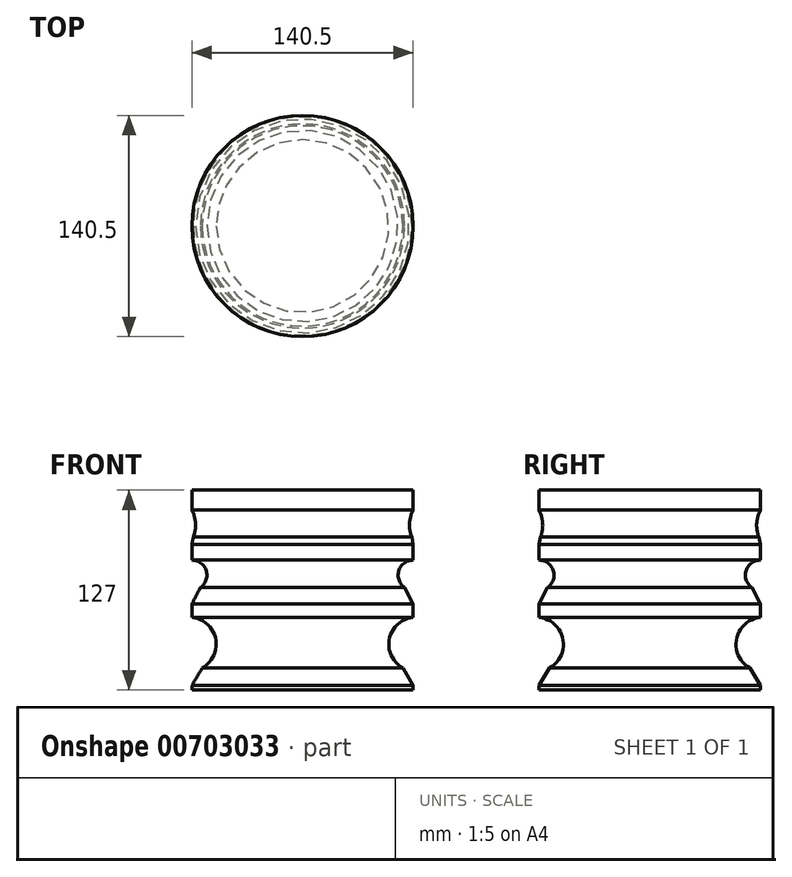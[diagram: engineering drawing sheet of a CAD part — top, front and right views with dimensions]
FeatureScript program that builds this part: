
annotation { "Feature Type Name" : "Feature", "Feature Type Description" : "" }
export const myFeature = defineFeature(function(context is Context, id is Id, definition is map)
    precondition{}
    {
        {
            var Q0;
            Q0=qCreatedBy(makeId("Front.planeOp"),FACE);
            var sketch = newSketch(context, id + "F0", { "sketchPlane" : qUnion([Q0])});
            skLineSegment(sketch, "E0", {"start": v(70.25, 0) * mm, "end": v(0, 0) * mm});
            skLineSegment(sketch, "E1", {"start": v(0, 0) * mm, "end": v(0, 127) * mm});
            skLineSegment(sketch, "E2", {"start": v(0, 127) * mm, "end": v(70.25, 127) * mm});
            skLineSegment(sketch, "E3", {"start": v(70.25, 127) * mm, "end": v(70.25, 114.3) * mm});
            skArc(sketch, "E4", {"start": v(70.25, 114.3) * mm, "mid": v(67.94, 104.78) * mm, "end": v(70.25, 95.25) * mm});
            skArc(sketch, "E5", {"start": v(70.25, 82.55) * mm, "mid": v(60.72, 73.03) * mm, "end": v(70.25, 63.5) * mm});
            skArc(sketch, "E6", {"start": v(70.25, 46.2) * mm, "mid": v(54.79, 29.12) * mm, "end": v(70.25, 12.04) * mm});
            skLineSegment(sketch, "E7.trimOffspring", {"start": v(70.25, 12.04) * mm, "end": v(70.25, 0) * mm});
            skLineSegment(sketch, "E8.trimOffspring", {"start": v(70.25, 63.5) * mm, "end": v(70.25, 46.2) * mm});
            skLineSegment(sketch, "E9.trimOffspring", {"start": v(70.25, 95.25) * mm, "end": v(70.25, 82.55) * mm});
            skSolve(sketch);
        }
        {
            var Q0;
            Q0=makeQuery(id+"F0.imprint","IMPRINT",FACE,{"disambiguationData":[TD([[makeQuery(id+"F0.imprint","IMPRINT",EDGE,{"derivedFrom":sQuery(id+"F0.wireOp",EDGE,"E0")}),-1.0]])]});
            var Q1;
            Q1=sQuery(id+"F0.wireOp",EDGE,"E1");
            revolve(context, id + "F1", {"surfaceOperationType" : NewSurfaceOperationType.NEW, "entities" : qUnion([Q0]), "axis" : qUnion([Q1]), "revolveType" : RevolveType.FULL});
        }
        {
            var Q0;
            Q0=makeQuery(id+"F1.opRevolve","SWEPT_EDGE",EDGE,{"disambiguationData":[OSD([sQuery(id+"F0.wireOp",EDGE,"E5"),sQuery(id+"F0.wireOp",EDGE,"E8.trimOffspring")])]});
            var Q1;
            Q1=makeQuery(id+"F1.opRevolve","SWEPT_EDGE",EDGE,{"disambiguationData":[OSD([sQuery(id+"F0.wireOp",EDGE,"E4"),sQuery(id+"F0.wireOp",EDGE,"E9.trimOffspring")])]});
            var Q2;
            Q2=makeQuery(id+"F1.opRevolve","SWEPT_EDGE",EDGE,{"disambiguationData":[OSD([sQuery(id+"F0.wireOp",EDGE,"E6"),sQuery(id+"F0.wireOp",EDGE,"E7.trimOffspring")])]});
            chamfer(context, id + "F2", {"entities" : qUnion([Q0, Q1, Q2]), "width" : 12.7 * mm, "tangentPropagation" : true});
        }
    });
